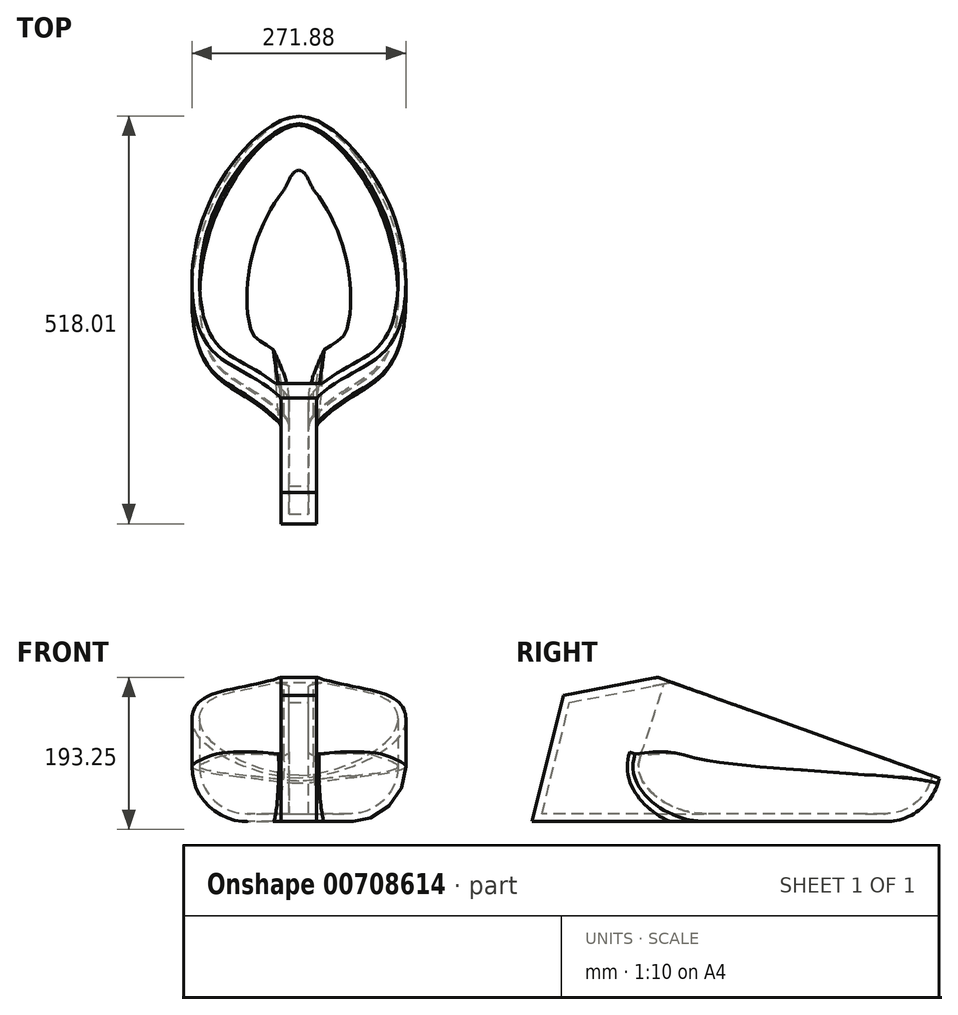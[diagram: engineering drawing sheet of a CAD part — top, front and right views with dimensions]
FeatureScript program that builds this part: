
annotation { "Feature Type Name" : "Feature", "Feature Type Description" : "" }
export const myFeature = defineFeature(function(context is Context, id is Id, definition is map)
    precondition{}
    {
        {
            var Q0;
            Q0=qCreatedBy(makeId("Right.planeOp"),FACE);
            var sketch = newSketch(context, id + "F0", { "sketchPlane" : qUnion([Q0])});
            skLineSegment(sketch, "E0", {"start": v(0, 0) * mm, "end": v(40, 160) * mm});
            skLineSegment(sketch, "E1", {"start": v(40, 160) * mm, "end": v(160, 183.25) * mm});
            skLineSegment(sketch, "E2", {"start": v(160, 183.25) * mm, "end": v(100, 0) * mm});
            skLineSegment(sketch, "E3", {"start": v(100, 0) * mm, "end": v(0, 0) * mm});
            skSolve(sketch);
        }
        {
            var Q0;
            Q0 = qSketchRegion(id + "F0", true);
            extrude(context, id + "F1", {"entities" : qUnion([Q0]), "oppositeDirection" : true, "depth" : 22.5 * mm, "offsetDistance" : 25 * mm});
        }
        {
            var Q0;
            Q0=qCreatedBy(makeId("Top.planeOp"),FACE);
            var sketch = newSketch(context, id + "F2", { "sketchPlane" : qUnion([Q0])});
            skLineSegment(sketch, "E4", {"start": v(-22.5, 100) * mm, "end": v(-115, 174.14) * mm, "construction": true});
            skLineSegment(sketch, "E5", {"start": v(-115, 174.14) * mm, "end": v(-115, 374.14) * mm, "construction": true});
            skLineSegment(sketch, "E6", {"start": v(-115, 374.14) * mm, "end": v(0, 500) * mm, "construction": true});
            skLineSegment(sketch, "E7", {"start": v(-22.5, 100) * mm, "end": v(0, 100) * mm});
            skLineSegment(sketch, "E8", {"start": v(0, 100) * mm, "end": v(0, 500) * mm});
            skFitSpline(sketch, "E9", {"points": [v(-22.5, 100) * mm, v(-115, 174.14) * mm, v(-115, 374.14) * mm, v(0, 500) * mm], "startDerivative": vector(-377.02, 389.04) * mm, "endDerivative": vector(312.85, 0) * mm});
            skPoint(sketch, "E10", {"position": v(-68.75, 137.07) * mm});
            skLineSegment(sketch, "E11", {"start": v(0, 500) * mm, "end": v(-147.27, 500) * mm, "construction": true});
            skSolve(sketch);
        }
        {
            var Q0;
            Q0 = qSketchRegion(id + "F2", true);
            var Q1;
            Q1=makeQuery(id+"F1.opExtrude","CAP_EDGE",EDGE,{"disambiguationData":[OSD([sQuery(id+"F0.wireOp",EDGE,"E2")])],"isStart":true});
            sweep(context, id + "F3", {"operationType" : NewBodyOperationType.ADD, "profiles" : qUnion([Q0]), "path" : qUnion([Q1])});
        }
        {
            var Q0;
            Q0=qCreatedBy(makeId("Right.planeOp"),FACE);
            var sketch = newSketch(context, id + "F4", { "sketchPlane" : qUnion([Q0])});
            skLineSegment(sketch, "E12", {"start": v(160, 183.25) * mm, "end": v(518, 55) * mm});
            skLineSegment(sketch, "E13", {"start": v(518, 55) * mm, "end": v(693.35, 211.91) * mm});
            skLineSegment(sketch, "E14", {"start": v(693.35, 211.91) * mm, "end": v(160, 183.25) * mm});
            skSolve(sketch);
        }
        {
            var Q0;
            Q0 = qSketchRegion(id + "F4", true);
            extrude(context, id + "F5", {"entities" : qUnion([Q0]), "operationType" : NewBodyOperationType.REMOVE, "oppositeDirection" : true, "depth" : 1000 * mm, "offsetDistance" : 25 * mm});
        }
        {
            var Q0;
            Q0=makeQuery(id+"F1.opExtrude","SWEPT_BODY",BODY,{"disambiguationData":[OSD([sQuery(id+"F0.wireOp",EDGE,"E0"),sQuery(id+"F0.wireOp",EDGE,"E1"),sQuery(id+"F0.wireOp",EDGE,"E2"),sQuery(id+"F0.wireOp",EDGE,"E3")])]});
            var Q1;
            Q1=qCreatedBy(makeId("Right.planeOp"),FACE);
            mirror(context, id + "F6", {"operationType" : NewBodyOperationType.ADD, "entities" : qUnion([Q0]), "mirrorPlane" : qUnion([Q1])});
        }
        {
            var Q0;
            Q0=makeQuery(id+"F6.opPattern","COPY",EDGE,{"derivedFrom":makeQuery(id+"F3.opSweep","CAP_EDGE",EDGE,{"disambiguationData":[OSD([sQuery(id+"F0.wireOp",EDGE,"E2"),sQuery(id+"F0.wireOp",EDGE,"E3"),sQuery(id+"F2.wireOp",EDGE,"E9")])],"isStart":true}),"instanceName":"1"});
            var Q1;
            Q1=makeQuery(id+"F3.opSweep","CAP_EDGE",EDGE,{"disambiguationData":[OSD([sQuery(id+"F0.wireOp",EDGE,"E2"),sQuery(id+"F0.wireOp",EDGE,"E3"),sQuery(id+"F2.wireOp",EDGE,"E9")])],"isStart":true});
            fillet(context, id + "F7", {"entities" : qUnion([Q0, Q1]), "radius" : 70 * mm, "tangentPropagation" : true, "allowEdgeOverflow" : false});
        }
        {
            var Q0;
            {var subQ0=sQuery(id+"F0.wireOp",EDGE,"E2");Q0=makeQuery(id+"F3.boolean.opBoolean","MERGE",EDGE,{"derivedFrom":[makeQuery(id+"F1.opExtrude","CAP_EDGE",EDGE,{"disambiguationData":[OSD([subQ0])],"isStart":false}),makeQuery(id+"F3.opSweep","SWEPT_EDGE",EDGE,{"disambiguationData":[OSD([subQ0,sQuery(id+"F2.wireOp",EDGE,"E7"),sQuery(id+"F2.wireOp",EDGE,"E9")])]})]});}
            var Q1;
            {var subQ0=sQuery(id+"F0.wireOp",EDGE,"E3");var subQ1=sQuery(id+"F0.wireOp",EDGE,"E2");Q1=makeQuery(id+"F7.opFillet","BLEND_EDGE",EDGE,{"blendedFrom":[makeQuery(id+"F3.opSweep","CAP_EDGE",EDGE,{"disambiguationData":[OSD([subQ1,subQ0,sQuery(id+"F2.wireOp",EDGE,"E9")])],"isStart":true}),makeQuery(id+"F1.opExtrude","CAP_FACE",FACE,{"disambiguationData":[OSD([sQuery(id+"F0.wireOp",EDGE,"E0"),sQuery(id+"F0.wireOp",EDGE,"E1"),subQ1,subQ0])],"isStart":false})],"blendedInto":[makeQuery(id+"F1.opExtrude","CAP_FACE",FACE,{"disambiguationData":[OSD([sQuery(id+"F0.wireOp",EDGE,"E0"),sQuery(id+"F0.wireOp",EDGE,"E1"),subQ1,subQ0])],"isStart":false})]});}
            var Q2;
            {var subQ0=sQuery(id+"F0.wireOp",EDGE,"E2");Q2=makeQuery(id+"F6.opPattern","COPY",EDGE,{"derivedFrom":makeQuery(id+"F3.boolean.opBoolean","MERGE",EDGE,{"derivedFrom":[makeQuery(id+"F1.opExtrude","CAP_EDGE",EDGE,{"disambiguationData":[OSD([subQ0])],"isStart":false}),makeQuery(id+"F3.opSweep","SWEPT_EDGE",EDGE,{"disambiguationData":[OSD([subQ0,sQuery(id+"F2.wireOp",EDGE,"E7"),sQuery(id+"F2.wireOp",EDGE,"E9")])]})]}),"instanceName":"1"});}
            var Q3;
            {var subQ0=sQuery(id+"F0.wireOp",EDGE,"E3");var subQ1=sQuery(id+"F0.wireOp",EDGE,"E2");Q3=makeQuery(id+"F7.opFillet","BLEND_EDGE",EDGE,{"blendedFrom":[makeQuery(id+"F6.opPattern","COPY",EDGE,{"derivedFrom":makeQuery(id+"F3.opSweep","CAP_EDGE",EDGE,{"disambiguationData":[OSD([subQ1,subQ0,sQuery(id+"F2.wireOp",EDGE,"E9")])],"isStart":true}),"instanceName":"1"}),makeQuery(id+"F6.opPattern","COPY",FACE,{"derivedFrom":makeQuery(id+"F1.opExtrude","CAP_FACE",FACE,{"disambiguationData":[OSD([sQuery(id+"F0.wireOp",EDGE,"E0"),sQuery(id+"F0.wireOp",EDGE,"E1"),subQ1,subQ0])],"isStart":false}),"instanceName":"1"})],"blendedInto":[makeQuery(id+"F6.opPattern","COPY",FACE,{"derivedFrom":makeQuery(id+"F1.opExtrude","CAP_FACE",FACE,{"disambiguationData":[OSD([sQuery(id+"F0.wireOp",EDGE,"E0"),sQuery(id+"F0.wireOp",EDGE,"E1"),subQ1,subQ0])],"isStart":false}),"instanceName":"1"})]});}
            fillet(context, id + "F8", {"entities" : qUnion([Q0, Q1, Q2, Q3]), "radius" : 10 * mm, "tangentPropagation" : true, "allowEdgeOverflow" : false});
        }
        {
            var Q0;
            {var subQ0=makeQuery(id+"F5.boolean.opBoolean","COPY",FACE,{"derivedFrom":makeQuery(id+"F5.opExtrude","SWEPT_FACE",FACE,{"disambiguationData":[OSD([sQuery(id+"F4.wireOp",EDGE,"E12")])]})});Q0=makeQuery(id+"F6.boolean.opBoolean","MERGE",FACE,{"derivedFrom":[subQ0,makeQuery(id+"F6.opPattern","COPY",FACE,{"derivedFrom":subQ0,"instanceName":"1"})]});}
            shell(context, id + "F9", {"entities" : qUnion([Q0]), "thickness" : 10 * mm});
        }
    });
